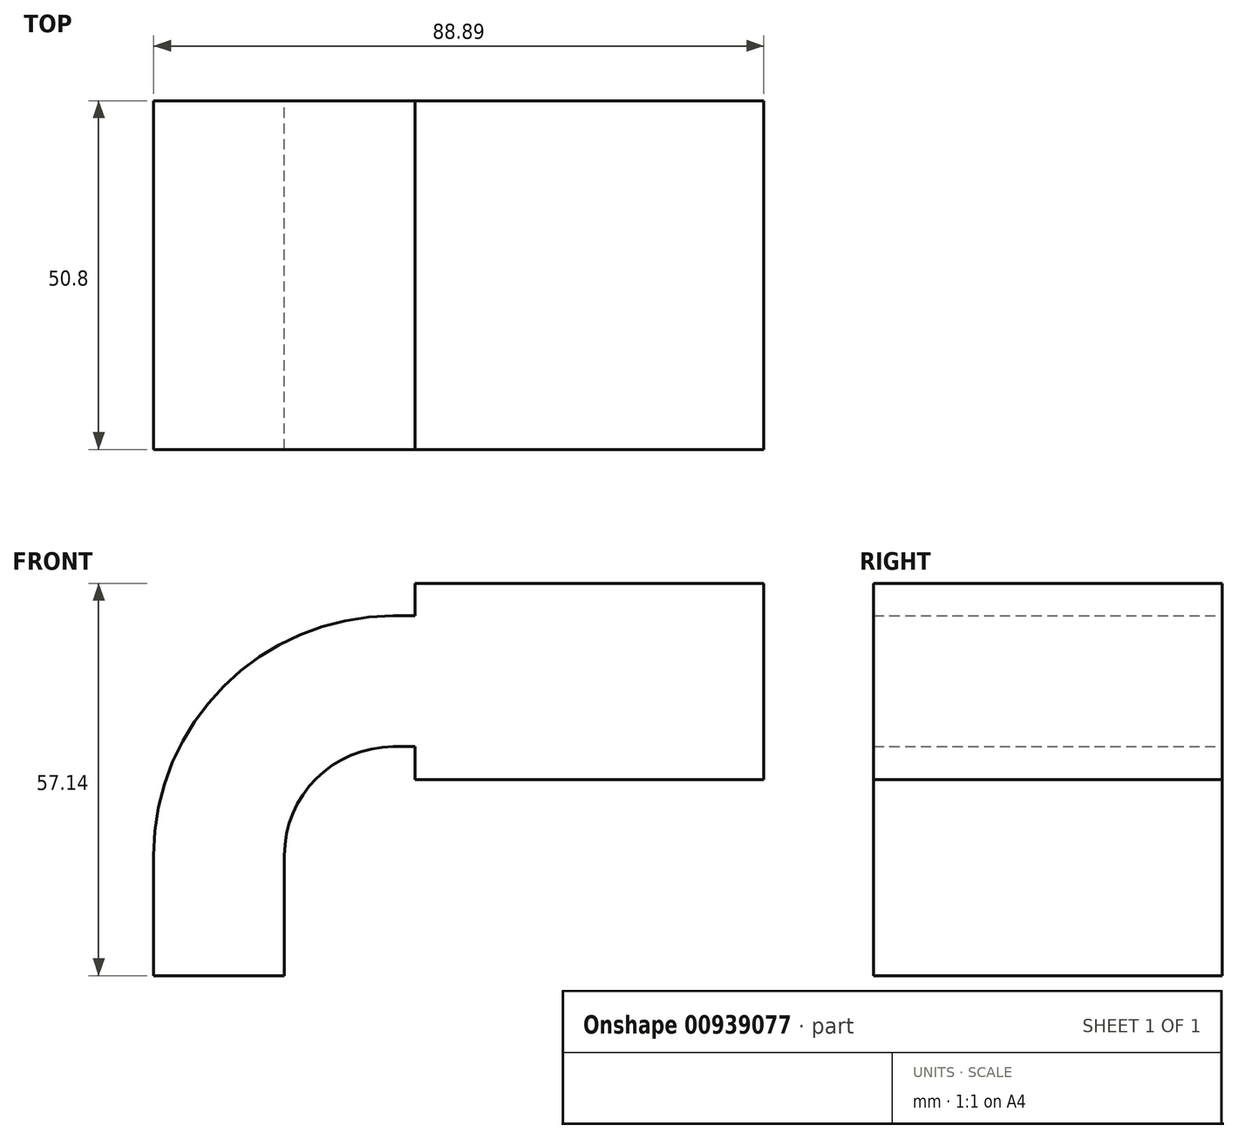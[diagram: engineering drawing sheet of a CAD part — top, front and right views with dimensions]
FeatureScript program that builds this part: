
annotation { "Feature Type Name" : "Feature", "Feature Type Description" : "" }
export const myFeature = defineFeature(function(context is Context, id is Id, definition is map)
    precondition{}
    {
        {
            var Q0;
            Q0=qCreatedBy(makeId("Front.planeOp"),FACE);
            var sketch = newSketch(context, id + "F0", { "sketchPlane" : qUnion([Q0])});
            skLineSegment(sketch, "E0.bottom", {"start": v(-41.28, 9.52) * mm, "end": v(41.27, 9.53) * mm});
            skLineSegment(sketch, "E0.top", {"start": v(-41.28, -9.53) * mm, "end": v(41.28, -9.53) * mm});
            skLineSegment(sketch, "E0.left", {"start": v(-41.28, 9.52) * mm, "end": v(-41.28, -9.53) * mm});
            skLineSegment(sketch, "E0.right", {"start": v(41.27, 9.53) * mm, "end": v(41.28, -9.52) * mm});
            skPoint(sketch, "E0.middle", {"position": v(0, 0) * mm});
            skLineSegment(sketch, "E1.bottom", {"start": v(60.32, 38.1) * mm, "end": v(111.12, 38.1) * mm});
            skLineSegment(sketch, "E1.top", {"start": v(60.32, 66.67) * mm, "end": v(111.12, 66.67) * mm});
            skLineSegment(sketch, "E1.left", {"start": v(60.32, 38.1) * mm, "end": v(60.32, 66.67) * mm});
            skLineSegment(sketch, "E1.right", {"start": v(111.12, 38.1) * mm, "end": v(111.12, 66.67) * mm});
            skPoint(sketch, "E1.middle", {"position": v(85.72, 52.39) * mm});
            skLineSegment(sketch, "E2", {"start": v(41.27, 9.53) * mm, "end": v(41.27, 27) * mm});
            skArc(sketch, "E3", {"start": v(41.27, 27) * mm, "mid": v(45.92, 38.23) * mm, "end": v(57.15, 42.88) * mm});
            skLineSegment(sketch, "E4", {"start": v(57.15, 42.88) * mm, "end": v(85.72, 42.88) * mm});
            skLineSegment(sketch, "E5.0", {"start": v(57.15, 61.93) * mm, "end": v(85.72, 61.93) * mm});
            skArc(sketch, "E5.1", {"start": v(22.22, 27) * mm, "mid": v(32.45, 51.7) * mm, "end": v(57.15, 61.93) * mm});
            skLineSegment(sketch, "E5.2", {"start": v(22.22, 9.53) * mm, "end": v(22.22, 27) * mm});
            skLineSegment(sketch, "E6", {"start": v(85.72, 38.1) * mm, "end": v(85.72, 66.67) * mm});
            skFitSpline(sketch, "E7", {"points": [v(-41.28, 9.52) * mm, v(57.15, 61.93) * mm], "startDerivative": vector(1.06, 58.52) * mm, "endDerivative": vector(171.45, -0.27) * mm});
            skSolve(sketch);
        }
        {
            var Q0;
            {var subQ0=sQuery(id+"F0.wireOp",EDGE,"E1.right");Q0=makeQuery(id+"F0.imprint","IMPRINT",FACE,{"disambiguationData":[TD([[makeQuery(id+"F0.imprint","IMPRINT",EDGE,{"derivedFrom":subQ0}),1.0]])]});}
            var Q1;
            {var subQ0=sQuery(id+"F0.wireOp",EDGE,"E4");var subQ1=sQuery(id+"F0.wireOp",EDGE,"E1.left");var subQ2=makeQuery(id+"F0.imprint","INTERSECT",VERTEX,{"derivedFrom":[subQ1,subQ0]});Q1=makeQuery(id+"F0.imprint","IMPRINT",FACE,{"disambiguationData":[TD([[makeQuery(id+"F0.imprint","IMPRINT",EDGE,{"disambiguationData":[TD([[subQ2,-1.0]])],"derivedFrom":subQ1}),-1.0]])]});}
            var Q2;
            {var subQ0=sQuery(id+"F0.wireOp",EDGE,"E1.left");var subQ1=sQuery(id+"F0.wireOp",EDGE,"E1.top");var subQ2=makeQuery(id+"F0.imprint","INTERSECT",VERTEX,{"derivedFrom":[subQ1,subQ0]});Q2=makeQuery(id+"F0.imprint","IMPRINT",FACE,{"disambiguationData":[TD([[makeQuery(id+"F0.imprint","IMPRINT",EDGE,{"disambiguationData":[TD([[subQ2,-1.0]])],"derivedFrom":subQ1}),-1.0]])]});}
            var Q3;
            {var subQ0=sQuery(id+"F0.wireOp",EDGE,"E1.left");var subQ1=sQuery(id+"F0.wireOp",EDGE,"E1.bottom");var subQ2=makeQuery(id+"F0.imprint","INTERSECT",VERTEX,{"derivedFrom":[subQ1,subQ0]});Q3=makeQuery(id+"F0.imprint","IMPRINT",FACE,{"disambiguationData":[TD([[makeQuery(id+"F0.imprint","IMPRINT",EDGE,{"disambiguationData":[TD([[subQ2,-1.0]])],"derivedFrom":subQ1}),1.0]])]});}
            var Q4;
            {var subQ1=sQuery(id+"F0.wireOp",EDGE,"E2");Q4=makeQuery(id+"F0.imprint","IMPRINT",FACE,{"disambiguationData":[TD([[makeQuery(id+"F0.imprint","IMPRINT",EDGE,{"derivedFrom":subQ1}),1.0]])]});}
            extrude(context, id + "F1", {"entities" : qUnion([Q0, Q1, Q2, Q3, Q4]), "endBound" : BoundingType.SYMMETRIC, "depth" : 50.8 * mm, "offsetDistance" : 25.4 * mm});
        }
    });
